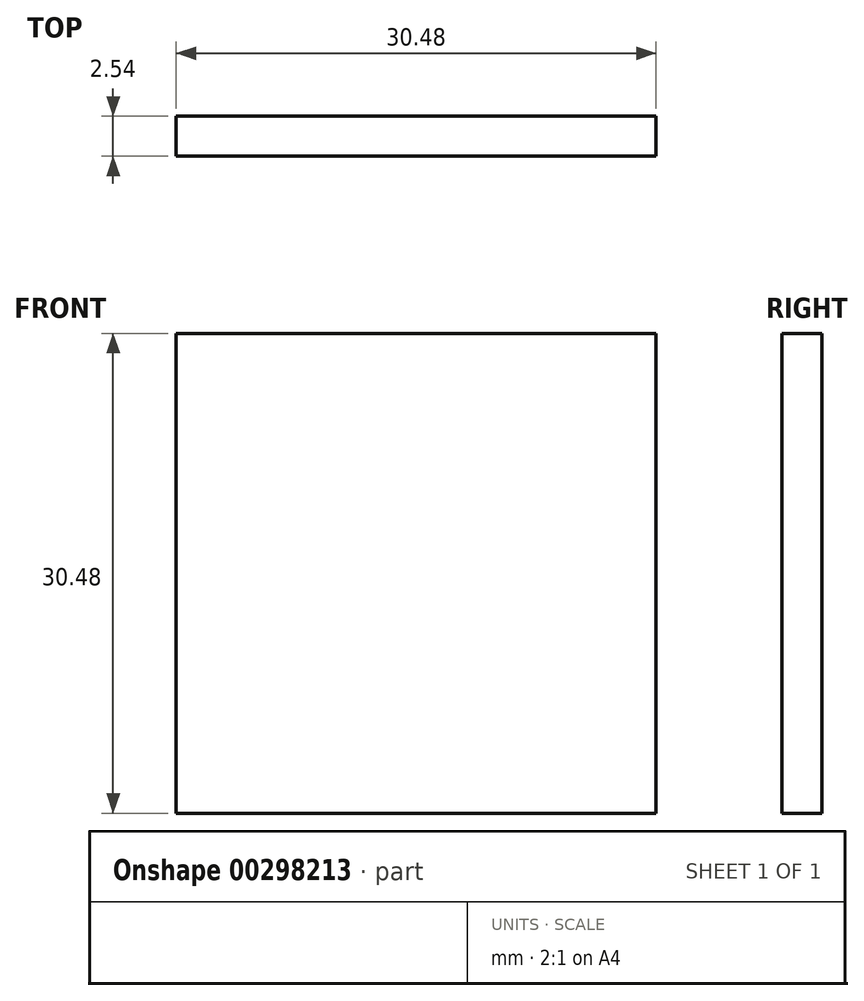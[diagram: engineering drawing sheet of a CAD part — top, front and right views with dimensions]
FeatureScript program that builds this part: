
annotation { "Feature Type Name" : "Feature", "Feature Type Description" : "" }
export const myFeature = defineFeature(function(context is Context, id is Id, definition is map)
    precondition{}
    {
        {
            var Q0;
            Q0=qCreatedBy(makeId("Front.planeOp"),FACE);
            var sketch = newSketch(context, id + "F0", { "sketchPlane" : qUnion([Q0])});
            skLineSegment(sketch, "E0.bottom", {"start": v(15.24, 15.24) * mm, "end": v(-15.24, 15.24) * mm});
            skLineSegment(sketch, "E0.top", {"start": v(15.24, -15.24) * mm, "end": v(-15.24, -15.24) * mm});
            skLineSegment(sketch, "E0.left", {"start": v(15.24, 15.24) * mm, "end": v(15.24, -15.24) * mm});
            skLineSegment(sketch, "E0.right", {"start": v(-15.24, 15.24) * mm, "end": v(-15.24, -15.24) * mm});
            skPoint(sketch, "E0.middle", {"position": v(0, 0) * mm});
            skSolve(sketch);
        }
        {
            var Q0;
            Q0=makeQuery(id+"F0.imprint","IMPRINT",FACE,{"disambiguationData":[TD([[makeQuery(id+"F0.imprint","IMPRINT",EDGE,{"derivedFrom":sQuery(id+"F0.wireOp",EDGE,"E0.bottom")}),1.0]])]});
            extrude(context, id + "F1", {"entities" : qUnion([Q0]), "depth" : 2.54 * mm});
        }
    });
